# Revit family: Safety & Protection_Barrier_UltiGroup_Guard Rail-GRIN 150
name_source: partatom
category: Generic Models
revit_build: Autodesk Revit Architecture 2016 (Build: 20150220_1215(x64)
units: mm (PartAtom-declared; Revit-internal decimal feet)

## family parameters
Always vertical = Yes
Can host rebar = No
Cut with Voids When Loaded = No
OmniClass Number = 23.40.70.17
OmniClass Title = Industrial and Manufacturing Equipment and Furnishings
Part Type = Normal
Room Calculation Point = No
Round Connector Dimension = Use Diameter
Shared = No
Work Plane-Based = No

## types (1)
- Type 1
    Base Plate Thickness = 12 mm  [stored 0.0393701 ft]
    Bolt hole depth = 80 mm
    Description = Impactable PVC Wall Protection Barrier
    End Extension - 15mm end cap = 185 mm  [stored 0.606955 ft]
    Extension End 1 = Yes
    Extension End 2 = Yes
    Fax = 07 846 2467
    InstallationGroup_ANZRS = 0
    Manufacturer = UltiGroup
    Metal Black = Metal Black
    Model = Wall Protection Barrier - GRIN 150
    ModifiedIssue_ANZRS = 0 $
    PVC Black = PVC Black
    PVC Yellow = PVC Yellow
    SS Bolts = SS Bolts
    Section Length = 1988 mm
    Send Message = http://ultigroup.co.nz
    Support 1 = Yes
    Support 2 = Yes
    URL = www.ultigroup.co.nz

note: [stored X ft] marks values corroborated as IEEE doubles in the binary element streams (Revit-internal decimal feet)

## geometry (parser evidence)
native form markers: Sweep x2
no freeform markers — native parametric forms only
